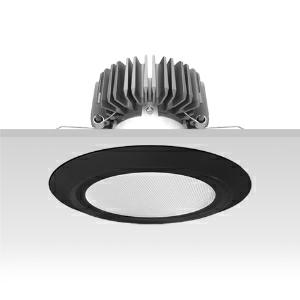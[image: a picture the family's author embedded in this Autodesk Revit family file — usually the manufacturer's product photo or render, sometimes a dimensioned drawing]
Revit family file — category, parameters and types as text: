
# Revit family: 3f_filippi_-_3f_reno_bianco_ampio_3f_filippi_-_30625_a01049_-_3f_reno_200_wh_2000-930_wide___smp_bk_fa0b
name_source: partatom
category: Lighting Fixtures
units: mm (PartAtom-declared; Revit-internal decimal feet)

## family parameters
Cut with Voids When Loaded = No
Host = Face
Light Source = No
Part Type = Normal
Room Calculation Point = No
Round Connector Dimension = Use Diameter
Shared = No

## types (1)
- 3F Filippi - 3F Reno Bianco Ampio (1 x LED, 1650 lm, 24 W, 3000 K)
    Apparent Load = 24 VA
    Approval mark = CE
    CIE Flux Codes = 74 92 98 100 100
    Color Rendering = 90
    Color Temperature = 3000 K
    Control Gear = Electronic ballast
    Default Elevation = 1800 mm
    Description = ILLUMINOTECHNICAL
Luminous efficiency 100% (DLOR 100%, ULOR 0%).
Initial luminous flux of the luminaire 1650 lm.
Direct symmetric wide distribution.
Installation Interdistance Transv.D = 1.06 x hu - Long.D = 1.04 x hu.
Average luminance <3000 cd/m² for radial angles >65°.
Tabular UGR (CIE 117 - 4H-8H; S=0.25H; 70/50/20): RUG 21.3 - 21.1.
Beam angle: 70° - 69°.
Luminous efficacy 69 lm/W.
Lifetime (L90/B10): 30000 h. (tq+25°C)
Lifetime (L85/B10): 50000 h. (tq+25°C)
Lifetime (L70/B10): 80000 h. (tq+25°C)
Sudden decreased luminous flux after 50000 hours: 0% (C0).
Photobiological safety in compliance with IEC/TR 62778: RG0 risk exempt, (IEC 62471).
In compliance with IEC/EN 62722-2-1 - IEC/EN 62717 standards.

SOURCE
Compact LED module 2000/930.
Energy efficiency class (UE 2019/2020 - UE 2019/2015): E.
CIE 13.3 Colour rendering index: CRI >90 (R9 >50%).
IES TM-30 Fidelity Index: Rf = 92 Rg = 101.
CCT nominal colour temperature 3000 K.
Colour initial tolerance (MacAdam): SDCM 3.
Zhaga Book 3 compliant.

MECHANICAL
Passive heat dissipator in die-casting aluminium, oversized, for optimum thermal management of the LED module.
Parabolic element with graduated/concentric rings in white polycarbonate.
Transparent external lens with glossy and satin differentiated surfaces, with a cooling and anti-insect system in methacrylate (PMMA).
Fastening spring clips in stainless steel.
Dimensions: diameter 226 mm, height 146 mm. Weight 1.01 kg.
IP44 protection degree for exposed part, IP20 for recessed part.
Mechanical strength to impacts IK05 (0.7 joule).
Glow-wire test resistance 650°C.

ELECTRICAL
Wiring on a separate unit.
Halogen Free electronic wiring 230V-50/60Hz, power factor 0.95, THD <25%, constant output current, SELV, class II, 1 driver.
Power of the luminaire 24 W.
ENEC - CE.
SAFE FLICKER: PstLM=<1 and SVM=<0.4 (IEC TR 61547-1 and IEC TR 63158), to ensure a more comfortable and safe light.
Luminaire compliant with EN 60598-2-22 for power supply from a centralised emergency system CPSS (Central Power Supply System), not incorporated in the luminaire - high risk areas excluded. The default power and flux are 100% in AC and 100% in DC.
Ambient temperature from 0°C to +25°C.
Temperature class T6 max 85°C.
Relative humidity UR: <85%.

INSTALLATION
Pull-up recessed fitting.
False ceiling carving: 200 mm.
All accessories dedicated to this product are available on the Catalog and on our website www.3F-Filippi.com.

ACCESSORIES
A01049 - Anti-glare microprismatic SMP diffuser in methacrylate (PMMA), locked and in line with the trim, in black polycarbonate.

APPLICATIONS
Suitable product for food production plants (HACCP), IFS (Food Version 6), BRC (GSFS Food Version 7).
Environments: architectural, commercial, exhibition areas, transit areas, corridors, shops, display windows, service areas.
In false ceilings with narrow voids.

WARNING
Luminaire designed for disposal/recycling at end-of-life.
Replaceable (LED only) light source by a professional. Replaceable control gear by a professional.
    Height = 0 mm  [stored 0 ft]
    Lamp = 1 x LED
    Lamp Light Flux = 1650 lm
    Lamp Power = 24 W
    Lamp count = 1
    Length = 226 mm
    Lifetime = 50000 h
    Luminous efficacy = 69 lm/W
    Manufacturer = 3F Filippi
    ModVariant = No
    Model = 3F Filippi - 30625+A01049 - 3F Reno 200 WH 2000-930 WIDE + SMP BK
    Mounting Place = Ceiling
    Mounting Type = Recessed
    Number of Poles = 1
    OnlyDefault = Yes
    Power Factor = 1
    Product Name = 3F Filippi - 3F Reno Bianco Ampio
    Product group = recessed luminaire
    ProductGroupID = 4
    Protection Class = Protection class II
    Protection Degree = IP 20
    RLX_Detail_Level = 1
    RLX_Emergency_Light_Flux = 0 lm
    RLX_Emergency_Type = 0
    RLX_Emergency_Type_DB = No
    RlxData = <blob elided: 97585 chars, md5=5095e6ba>
    Socket = socket
    Standby Power = 0 W
    System Light Flux = 1650 lm
    System Power = 24 W
    Type Comments = Product without accessories
    Type Image = 3ffilippi_3f_reno_200_bk_vs_smp.jpg
    URL = http://relux.com
    VarID = ---
    Voltage = 0 V
    Weight = 0.00 kg
    Width = 0 mm  [stored 0 ft]

note: [stored X ft] marks values corroborated as IEEE doubles in the binary element streams (Revit-internal decimal feet)

## geometry (parser evidence)
native form markers: Blend x4, Sweep x11
no freeform markers — native parametric forms only
